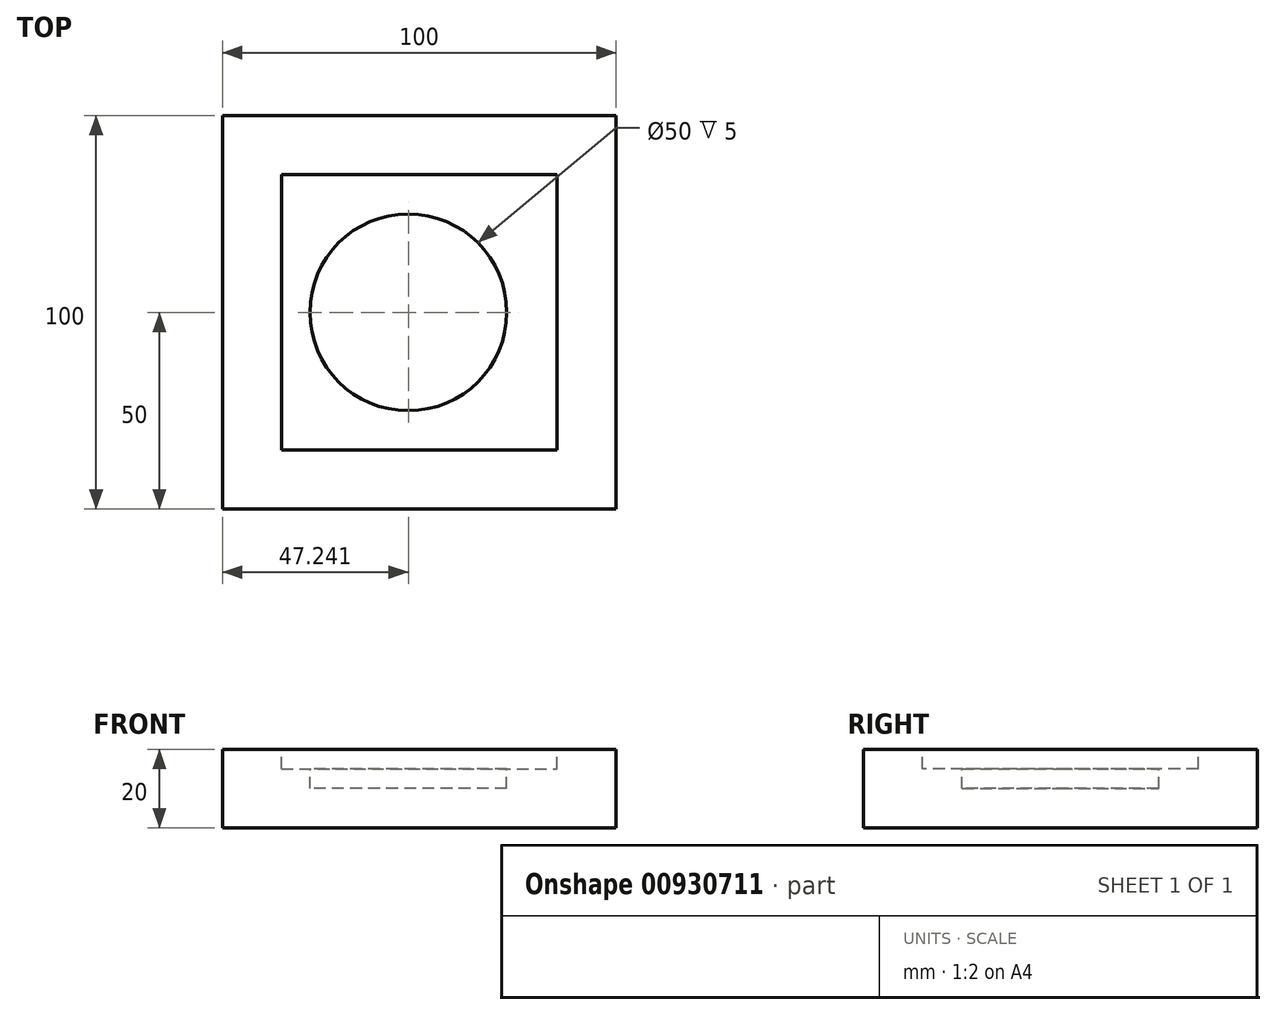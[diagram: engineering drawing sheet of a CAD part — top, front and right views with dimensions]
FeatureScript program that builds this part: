
annotation { "Feature Type Name" : "Feature", "Feature Type Description" : "" }
export const myFeature = defineFeature(function(context is Context, id is Id, definition is map)
    precondition{}
    {
        {
            var Q0;
            Q0=qCreatedBy(makeId("Top.planeOp"),FACE);
            var sketch = newSketch(context, id + "F0", { "sketchPlane" : qUnion([Q0])});
            skLineSegment(sketch, "E0.bottom", {"start": v(50, 50) * mm, "end": v(-50, 50) * mm});
            skLineSegment(sketch, "E0.top", {"start": v(50, -50) * mm, "end": v(-50, -50) * mm});
            skLineSegment(sketch, "E0.left", {"start": v(50, 50) * mm, "end": v(50, -50) * mm});
            skLineSegment(sketch, "E0.right", {"start": v(-50, 50) * mm, "end": v(-50, -50) * mm});
            skPoint(sketch, "E0.middle", {"position": v(0, 0) * mm});
            skSolve(sketch);
        }
        {
            var Q0;
            Q0=makeQuery(id+"F0.imprint","IMPRINT",FACE,{"disambiguationData":[TD([[makeQuery(id+"F0.imprint","IMPRINT",EDGE,{"derivedFrom":sQuery(id+"F0.wireOp",EDGE,"E0.bottom")}),1.0]])]});
            extrude(context, id + "F1", {"entities" : qUnion([Q0]), "depth" : 20 * mm, "offsetDistance" : 25 * mm});
        }
        {
            var Q0;
            Q0=makeQuery(id+"F1.opExtrude","CAP_FACE",FACE,{"disambiguationData":[OSD([sQuery(id+"F0.wireOp",EDGE,"E0.bottom"),sQuery(id+"F0.wireOp",EDGE,"E0.top"),sQuery(id+"F0.wireOp",EDGE,"E0.left"),sQuery(id+"F0.wireOp",EDGE,"E0.right")])],"isStart":false});
            var sketch = newSketch(context, id + "F2", { "sketchPlane" : qUnion([Q0])});
            skCircle(sketch, "E1", {"center": v(-2.76, 0) * mm, "radius": 25 * mm});
            skSolve(sketch);
        }
        {
            var Q0;
            Q0=makeQuery(id+"F2.imprint","IMPRINT",FACE,{"disambiguationData":[TD([[makeQuery(id+"F2.imprint","IMPRINT",EDGE,{"derivedFrom":sQuery(id+"F2.wireOp",EDGE,"E1")}),1.0]])]});
            extrude(context, id + "F3", {"entities" : qUnion([Q0]), "operationType" : NewBodyOperationType.REMOVE, "oppositeDirection" : true, "depth" : 10 * mm, "offsetDistance" : 25 * mm});
        }
        {
            var Q0;
            Q0=makeQuery(id+"F1.opExtrude","CAP_FACE",FACE,{"disambiguationData":[OSD([sQuery(id+"F0.wireOp",EDGE,"E0.bottom"),sQuery(id+"F0.wireOp",EDGE,"E0.top"),sQuery(id+"F0.wireOp",EDGE,"E0.left"),sQuery(id+"F0.wireOp",EDGE,"E0.right")])],"isStart":false});
            var sketch = newSketch(context, id + "F4", { "sketchPlane" : qUnion([Q0])});
            skLineSegment(sketch, "E2.bottom", {"start": v(-35, 35) * mm, "end": v(35, 35) * mm});
            skLineSegment(sketch, "E2.top", {"start": v(-35, -35) * mm, "end": v(35, -35) * mm});
            skLineSegment(sketch, "E2.left", {"start": v(-35, 35) * mm, "end": v(-35, -35) * mm});
            skLineSegment(sketch, "E2.right", {"start": v(35, 35) * mm, "end": v(35, -35) * mm});
            skPoint(sketch, "E2.middle", {"position": v(0, 0) * mm});
            skSolve(sketch);
        }
        {
            var Q0;
            Q0=makeQuery(id+"F4.imprint","IMPRINT",FACE,{"disambiguationData":[TD([[makeQuery(id+"F4.imprint","IMPRINT",EDGE,{"derivedFrom":sQuery(id+"F4.wireOp",EDGE,"E2.bottom")}),-1.0]])]});
            extrude(context, id + "F5", {"entities" : qUnion([Q0]), "operationType" : NewBodyOperationType.REMOVE, "oppositeDirection" : true, "depth" : 5 * mm, "offsetDistance" : 25 * mm});
        }
    });
